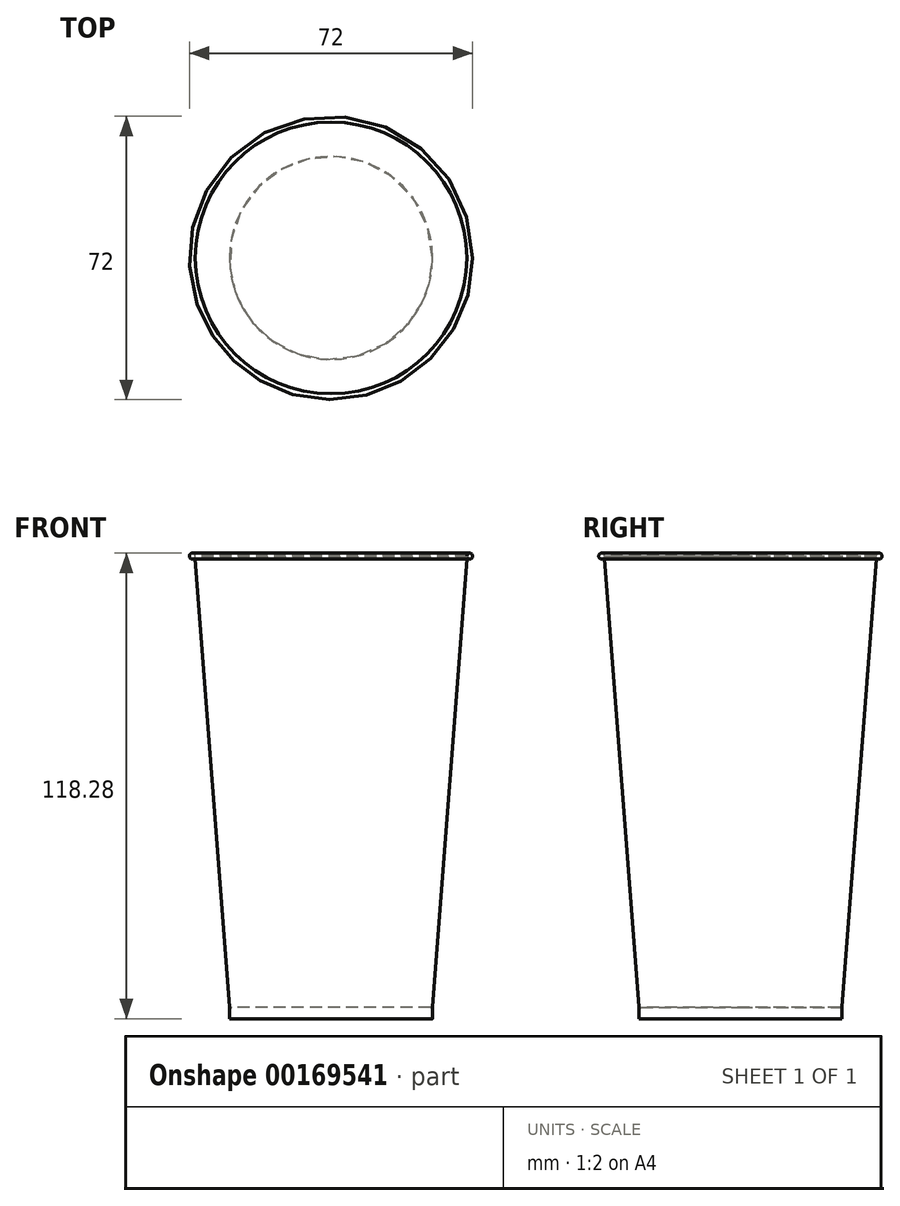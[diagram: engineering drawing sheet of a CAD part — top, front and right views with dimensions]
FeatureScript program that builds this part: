
annotation { "Feature Type Name" : "Feature", "Feature Type Description" : "" }
export const myFeature = defineFeature(function(context is Context, id is Id, definition is map)
    precondition{}
    {
        {
            var Q0;
            Q0=qCreatedBy(makeId("Front.planeOp"),FACE);
            var sketch = newSketch(context, id + "F0", { "sketchPlane" : qUnion([Q0])});
            skCircle(sketch, "E0", {"center": v(35.25, 0) * mm, "radius": 0.75 * mm});
            skLineSegment(sketch, "E1", {"start": v(0, 35.51) * mm, "end": v(0, -64.49) * mm, "construction": true});
            skLineSegment(sketch, "E2", {"start": v(34.5, 0) * mm, "end": v(25.71, -114.63) * mm});
            skLineSegment(sketch, "E3", {"start": v(34.56, -0.3) * mm, "end": v(25.8, -114.72) * mm});
            skLineSegment(sketch, "E4", {"start": v(0, -114.63) * mm, "end": v(25.71, -114.63) * mm});
            skLineSegment(sketch, "E5", {"start": v(0, -114.72) * mm, "end": v(25.7, -114.72) * mm});
            skLineSegment(sketch, "E6", {"start": v(0, -114.63) * mm, "end": v(0, -114.72) * mm});
            skLineSegment(sketch, "E7", {"start": v(25.8, -114.72) * mm, "end": v(25.8, -117.53) * mm});
            skLineSegment(sketch, "E8", {"start": v(25.7, -114.72) * mm, "end": v(25.77, -117.53) * mm});
            skLineSegment(sketch, "E9", {"start": v(25.77, -117.53) * mm, "end": v(25.8, -117.53) * mm});
            skArc(sketch, "E10", {"start": v(25.77, -117.53) * mm, "mid": v(25.78, -117.54) * mm, "end": v(25.8, -117.53) * mm});
            skSolve(sketch);
        }
        {
            var Q0;
            {var subQ1=sQuery(id+"F0.wireOp",EDGE,"E2");Q0=makeQuery(id+"F0.imprint","IMPRINT",FACE,{"disambiguationData":[TD([[makeQuery(id+"F0.imprint","IMPRINT",EDGE,{"derivedFrom":subQ1}),1.0]])]});}
            var Q1;
            {var subQ0=sQuery(id+"F0.wireOp",EDGE,"E0");var subQ1=makeQuery(id+"F0.imprint","INTERSECT",VERTEX,{"derivedFrom":[subQ0,sQuery(id+"F0.wireOp",EDGE,"E2")]});Q1=makeQuery(id+"F0.imprint","IMPRINT",FACE,{"disambiguationData":[TD([[makeQuery(id+"F0.imprint","IMPRINT",EDGE,{"disambiguationData":[TD([[subQ1,-1.0]])],"derivedFrom":subQ0}),1.0]])]});}
            var Q2;
            Q2=sQuery(id+"F0.wireOp",EDGE,"E1");
            revolve(context, id + "F1", {"entities" : qUnion([Q0, Q1]), "axis" : qUnion([Q2]), "revolveType" : RevolveType.FULL});
        }
        {
            var Q0;
            Q0=makeQuery(id+"F1.opRevolve","SWEPT_EDGE",EDGE,{"disambiguationData":[OSD([sQuery(id+"F0.wireOp",EDGE,"E2"),sQuery(id+"F0.wireOp",EDGE,"E4")])]});
            fillet(context, id + "F2", {"entities" : qUnion([Q0]), "radius" : 0.5 * mm, "tangentPropagation" : true, "allowEdgeOverflow" : false});
        }
        {
            var Q0;
            Q0=makeQuery(id+"F1.opRevolve","SWEPT_EDGE",EDGE,{"disambiguationData":[OSD([sQuery(id+"F0.wireOp",EDGE,"E5"),sQuery(id+"F0.wireOp",EDGE,"E8")])]});
            fillet(context, id + "F3", {"entities" : qUnion([Q0]), "radius" : 0.5 * mm, "tangentPropagation" : true, "allowEdgeOverflow" : false});
        }
        {
            var Q0;
            Q0=makeQuery(id+"F1.opRevolve","SWEPT_EDGE",EDGE,{"disambiguationData":[OSD([sQuery(id+"F0.wireOp",EDGE,"E3"),sQuery(id+"F0.wireOp",EDGE,"E7")])]});
            fillet(context, id + "F4", {"entities" : qUnion([Q0]), "radius" : 5 * mm, "tangentPropagation" : true, "allowEdgeOverflow" : false});
        }
    });
